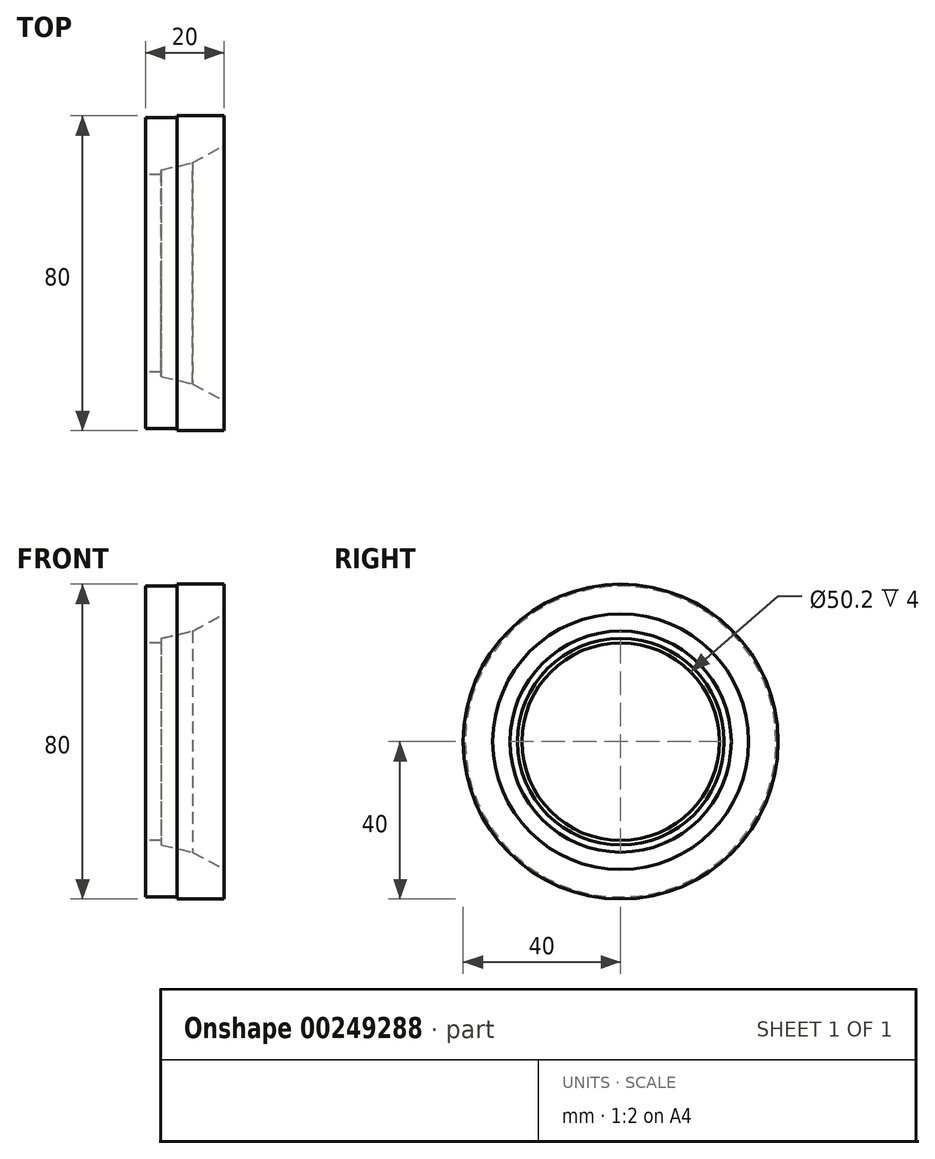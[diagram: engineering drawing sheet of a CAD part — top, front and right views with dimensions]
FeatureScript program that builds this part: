
annotation { "Feature Type Name" : "Feature", "Feature Type Description" : "" }
export const myFeature = defineFeature(function(context is Context, id is Id, definition is map)
    precondition{}
    {
        {
            var Q0;
            Q0=qCreatedBy(makeId("Front.planeOp"),FACE);
            var sketch = newSketch(context, id + "F0", { "sketchPlane" : qUnion([Q0])});
            skLineSegment(sketch, "E0", {"start": v(0, 0) * mm, "end": v(22.58, 0) * mm, "construction": true});
            skLineSegment(sketch, "E1", {"start": v(0, 40) * mm, "end": v(20, 40) * mm});
            skLineSegment(sketch, "E2", {"start": v(20, 40) * mm, "end": v(20, 32.5) * mm});
            skLineSegment(sketch, "E3", {"start": v(4, 26.25) * mm, "end": v(4, 25.1) * mm});
            skLineSegment(sketch, "E4", {"start": v(4, 25.1) * mm, "end": v(0, 25.1) * mm});
            skLineSegment(sketch, "E5", {"start": v(0, 25.1) * mm, "end": v(0, 40) * mm});
            skLineSegment(sketch, "E6", {"start": v(4, 26.25) * mm, "end": v(14, 28.56) * mm, "construction": true});
            skLineSegment(sketch, "E7", {"start": v(4, 26.25) * mm, "end": v(12, 28.1) * mm});
            skLineSegment(sketch, "E8", {"start": v(12, 28.1) * mm, "end": v(20, 32.5) * mm});
            skSolve(sketch);
        }
        {
            var Q0;
            Q0=makeQuery(id+"F0.imprint","IMPRINT",FACE,{"disambiguationData":[TD([[makeQuery(id+"F0.imprint","IMPRINT",EDGE,{"derivedFrom":sQuery(id+"F0.wireOp",EDGE,"E1")}),-1.0]])]});
            var Q1;
            Q1=sQuery(id+"F0.wireOp",EDGE,"E0");
            revolve(context, id + "F1", {"surfaceOperationType" : NewSurfaceOperationType.NEW, "entities" : qUnion([Q0]), "axis" : qUnion([Q1]), "revolveType" : RevolveType.FULL});
        }
        {
            var Q0;
            Q0=qCreatedBy(makeId("Front.planeOp"),FACE);
            var sketch = newSketch(context, id + "F2", { "sketchPlane" : qUnion([Q0])});
            skLineSegment(sketch, "E9", {"start": v(0, 0) * mm, "end": v(35.58, 0) * mm, "construction": true});
            skLineSegment(sketch, "E10", {"start": v(0, 40) * mm, "end": v(8, 40) * mm});
            skLineSegment(sketch, "E11", {"start": v(8, 40) * mm, "end": v(8, 39.5) * mm});
            skLineSegment(sketch, "E12", {"start": v(8, 39.5) * mm, "end": v(0, 39.5) * mm});
            skPoint(sketch, "E13.0.start.orphan", {"position": v(0, -40) * mm});
            skLineSegment(sketch, "E14", {"start": v(0, 40) * mm, "end": v(0, 39.5) * mm});
            skSolve(sketch);
        }
        {
            var Q0;
            Q0=makeQuery(id+"F2.imprint","IMPRINT",FACE,{"disambiguationData":[TD([[makeQuery(id+"F2.imprint","IMPRINT",EDGE,{"derivedFrom":sQuery(id+"F2.wireOp",EDGE,"E10")}),-1.0]])]});
            var Q1;
            Q1=sQuery(id+"F2.wireOp",EDGE,"E9");
            revolve(context, id + "F3", {"operationType" : NewBodyOperationType.REMOVE, "surfaceOperationType" : NewSurfaceOperationType.NEW, "entities" : qUnion([Q0]), "axis" : qUnion([Q1]), "revolveType" : RevolveType.FULL, "oppositeDirection" : true});
        }
    });
